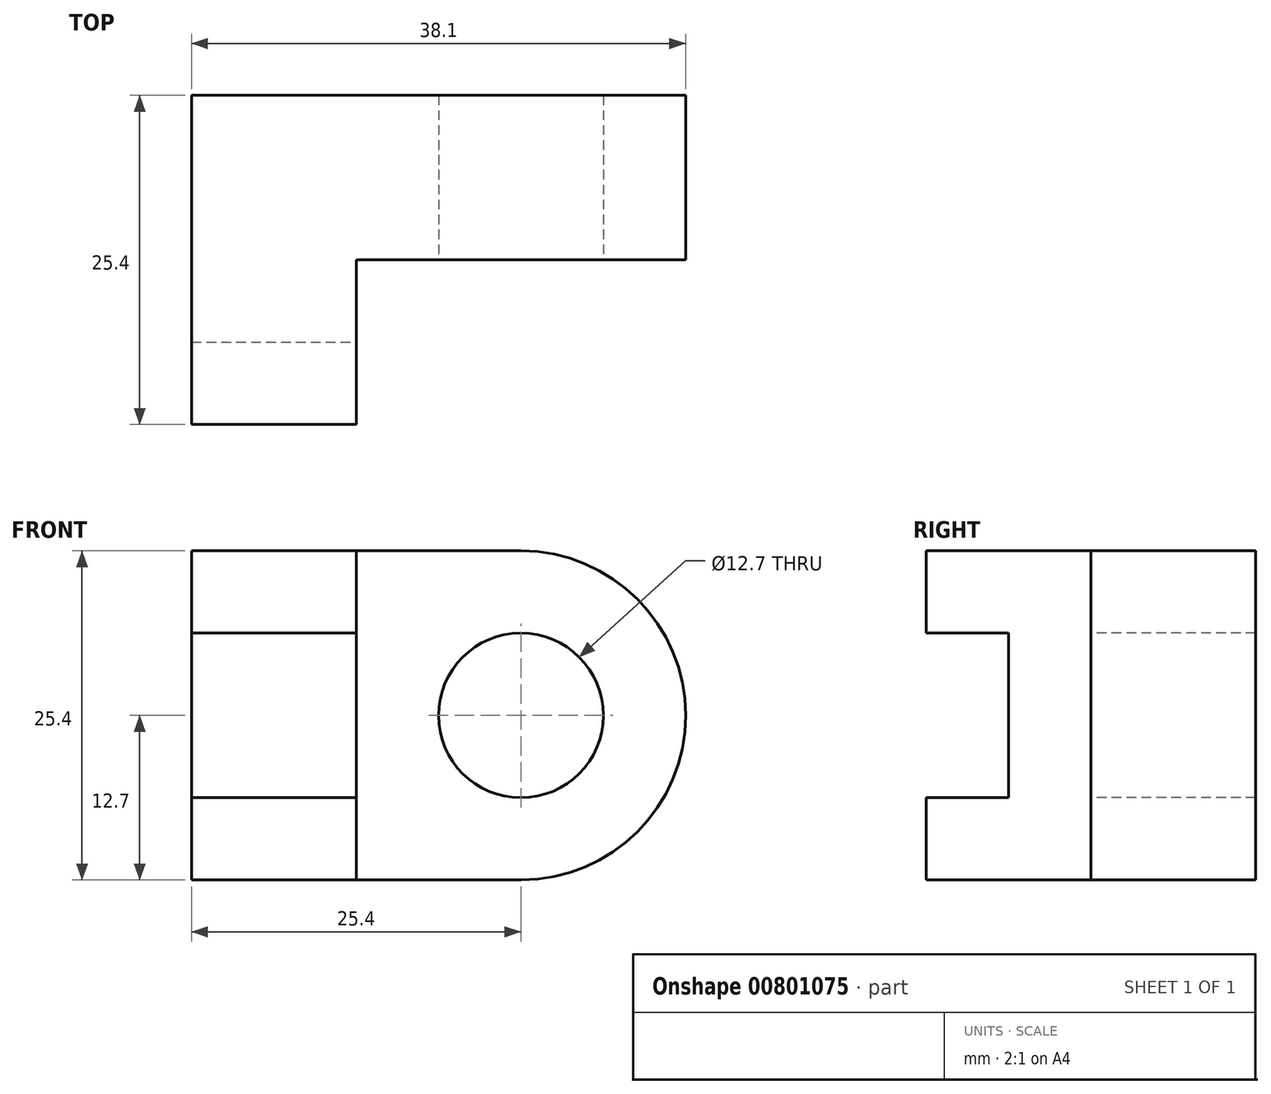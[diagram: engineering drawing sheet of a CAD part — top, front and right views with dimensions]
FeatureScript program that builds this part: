
annotation { "Feature Type Name" : "Feature", "Feature Type Description" : "" }
export const myFeature = defineFeature(function(context is Context, id is Id, definition is map)
    precondition{}
    {
        {
            var Q0;
            Q0=qCreatedBy(makeId("Front.planeOp"),FACE);
            var sketch = newSketch(context, id + "F0", { "sketchPlane" : qUnion([Q0])});
            skLineSegment(sketch, "E0", {"start": v(0, 0) * mm, "end": v(38.1, 0) * mm});
            skLineSegment(sketch, "E1", {"start": v(38.1, 0) * mm, "end": v(38.1, 25.4) * mm});
            skLineSegment(sketch, "E2", {"start": v(38.1, 25.4) * mm, "end": v(0, 25.4) * mm});
            skLineSegment(sketch, "E3", {"start": v(0, 25.4) * mm, "end": v(0, 0) * mm});
            skSolve(sketch);
        }
        {
            var Q0;
            Q0 = qSketchRegion(id + "F0", true);
            extrude(context, id + "F1", {"entities" : qUnion([Q0]), "depth" : 25.4 * mm, "offsetDistance" : 25.4 * mm});
        }
        {
            var Q0;
            Q0=makeQuery(id+"F1.opExtrude","SWEPT_FACE",FACE,{"disambiguationData":[OSD([sQuery(id+"F0.wireOp",EDGE,"E1")])]});
            var sketch = newSketch(context, id + "F2", { "sketchPlane" : qUnion([Q0])});
            skLineSegment(sketch, "E4", {"start": v(-25.4, 25.4) * mm, "end": v(-12.7, 25.4) * mm});
            skLineSegment(sketch, "E5", {"start": v(-12.7, 25.4) * mm, "end": v(-12.7, 0) * mm});
            skLineSegment(sketch, "E6", {"start": v(-12.7, 0) * mm, "end": v(-25.4, 0) * mm});
            skLineSegment(sketch, "E7", {"start": v(-25.4, 0) * mm, "end": v(-25.4, 25.4) * mm});
            skSolve(sketch);
        }
        {
            var Q0;
            Q0=makeQuery(id+"F2.imprint","IMPRINT",FACE,{"disambiguationData":[TD([[makeQuery(id+"F2.imprint","IMPRINT",EDGE,{"derivedFrom":sQuery(id+"F2.wireOp",EDGE,"E4")}),-1.0]])]});
            extrude(context, id + "F3", {"entities" : qUnion([Q0]), "operationType" : NewBodyOperationType.REMOVE, "oppositeDirection" : true, "depth" : 25.4 * mm, "offsetDistance" : 25.4 * mm});
        }
        {
            var Q0;
            Q0=makeQuery(id+"F3.boolean.opBoolean","COPY",FACE,{"derivedFrom":makeQuery(id+"F3.opExtrude","CAP_FACE",FACE,{"disambiguationData":[OSD([sQuery(id+"F2.wireOp",EDGE,"E4"),sQuery(id+"F2.wireOp",EDGE,"E5"),sQuery(id+"F2.wireOp",EDGE,"E6"),sQuery(id+"F2.wireOp",EDGE,"E7")])],"isStart":false})});
            var sketch = newSketch(context, id + "F4", { "sketchPlane" : qUnion([Q0])});
            skLineSegment(sketch, "E8", {"start": v(-25.4, 19.05) * mm, "end": v(-19.05, 19.05) * mm});
            skLineSegment(sketch, "E9", {"start": v(-19.05, 19.05) * mm, "end": v(-19.05, 6.35) * mm});
            skLineSegment(sketch, "E10", {"start": v(-19.05, 6.35) * mm, "end": v(-25.4, 6.35) * mm});
            skLineSegment(sketch, "E11", {"start": v(-25.4, 6.35) * mm, "end": v(-25.4, 19.05) * mm});
            skSolve(sketch);
        }
        {
            var Q0;
            Q0=makeQuery(id+"F4.imprint","IMPRINT",FACE,{"disambiguationData":[TD([[makeQuery(id+"F4.imprint","IMPRINT",EDGE,{"derivedFrom":sQuery(id+"F4.wireOp",EDGE,"E8")}),-1.0]])]});
            extrude(context, id + "F5", {"entities" : qUnion([Q0]), "operationType" : NewBodyOperationType.REMOVE, "oppositeDirection" : true, "depth" : 12.7 * mm, "offsetDistance" : 25.4 * mm});
        }
        {
            var Q0;
            Q0=makeQuery(id+"F3.boolean.opBoolean","COPY",FACE,{"derivedFrom":makeQuery(id+"F3.opExtrude","SWEPT_FACE",FACE,{"disambiguationData":[OSD([sQuery(id+"F2.wireOp",EDGE,"E5")])]})});
            var sketch = newSketch(context, id + "F6", { "sketchPlane" : qUnion([Q0])});
            skLineSegment(sketch, "E12", {"start": v(12.7, 0) * mm, "end": v(12.7, 12.7) * mm, "construction": true});
            skLineSegment(sketch, "E13", {"start": v(12.7, 12.7) * mm, "end": v(25.4, 12.7) * mm, "construction": true});
            skCircle(sketch, "E14", {"center": v(25.4, 12.7) * mm, "radius": 6.35 * mm});
            skSolve(sketch);
        }
        {
            var Q0;
            Q0 = qSketchRegion(id + "F6", true);
            extrude(context, id + "F7", {"entities" : qUnion([Q0]), "operationType" : NewBodyOperationType.REMOVE, "oppositeDirection" : true, "depth" : 12.7 * mm, "offsetDistance" : 25.4 * mm});
        }
        {
            var Q0;
            Q0=makeQuery(id+"F3.boolean.opBoolean","COPY",FACE,{"derivedFrom":makeQuery(id+"F3.opExtrude","SWEPT_FACE",FACE,{"disambiguationData":[OSD([sQuery(id+"F2.wireOp",EDGE,"E5")])]})});
            var sketch = newSketch(context, id + "F8", { "sketchPlane" : qUnion([Q0])});
            skLineSegment(sketch, "E15", {"start": v(12.7, 25.4) * mm, "end": v(25.4, 25.4) * mm, "construction": true});
            skLineSegment(sketch, "E16", {"start": v(12.7, 0) * mm, "end": v(25.4, 0) * mm, "construction": true});
            skArc(sketch, "E17", {"start": v(25.4, 0) * mm, "mid": v(38.1, 12.7) * mm, "end": v(25.4, 25.4) * mm});
            skSolve(sketch);
        }
        {
            var Q0;
            {var subQ0=sQuery(id+"F8.wireOp",EDGE,"E17");var subQ1=sQuery(id+"F2.wireOp",EDGE,"E5");var subQ4=makeQuery(id+"F3.boolean.opBoolean","COPY",EDGE,{"derivedFrom":makeQuery(id+"F3.opExtrude","CAP_EDGE",EDGE,{"disambiguationData":[OSD([subQ1])],"isStart":true})});var subQ5=makeQuery(id+"F8.imprint","INTERSECT",VERTEX,{"derivedFrom":[subQ4,subQ0]});Q0=makeQuery(id+"F8.imprint","IMPRINT",FACE,{"disambiguationData":[TD([[makeQuery(id+"F8.imprint","IMPRINT",EDGE,{"disambiguationData":[TD([[subQ5,-1.0]])],"derivedFrom":subQ0}),-1.0]])]});}
            var Q1;
            {var subQ0=sQuery(id+"F8.wireOp",EDGE,"E17");var subQ1=sQuery(id+"F2.wireOp",EDGE,"E5");var subQ4=makeQuery(id+"F3.boolean.opBoolean","COPY",EDGE,{"derivedFrom":makeQuery(id+"F3.opExtrude","CAP_EDGE",EDGE,{"disambiguationData":[OSD([subQ1])],"isStart":true})});var subQ5=makeQuery(id+"F8.imprint","INTERSECT",VERTEX,{"derivedFrom":[subQ4,subQ0]});Q1=makeQuery(id+"F8.imprint","IMPRINT",FACE,{"disambiguationData":[TD([[makeQuery(id+"F8.imprint","IMPRINT",EDGE,{"disambiguationData":[TD([[subQ5,1.0]])],"derivedFrom":subQ0}),-1.0]])]});}
            extrude(context, id + "F9", {"entities" : qUnion([Q0, Q1]), "operationType" : NewBodyOperationType.REMOVE, "oppositeDirection" : true, "depth" : 25.4 * mm, "offsetDistance" : 25.4 * mm});
        }
    });
